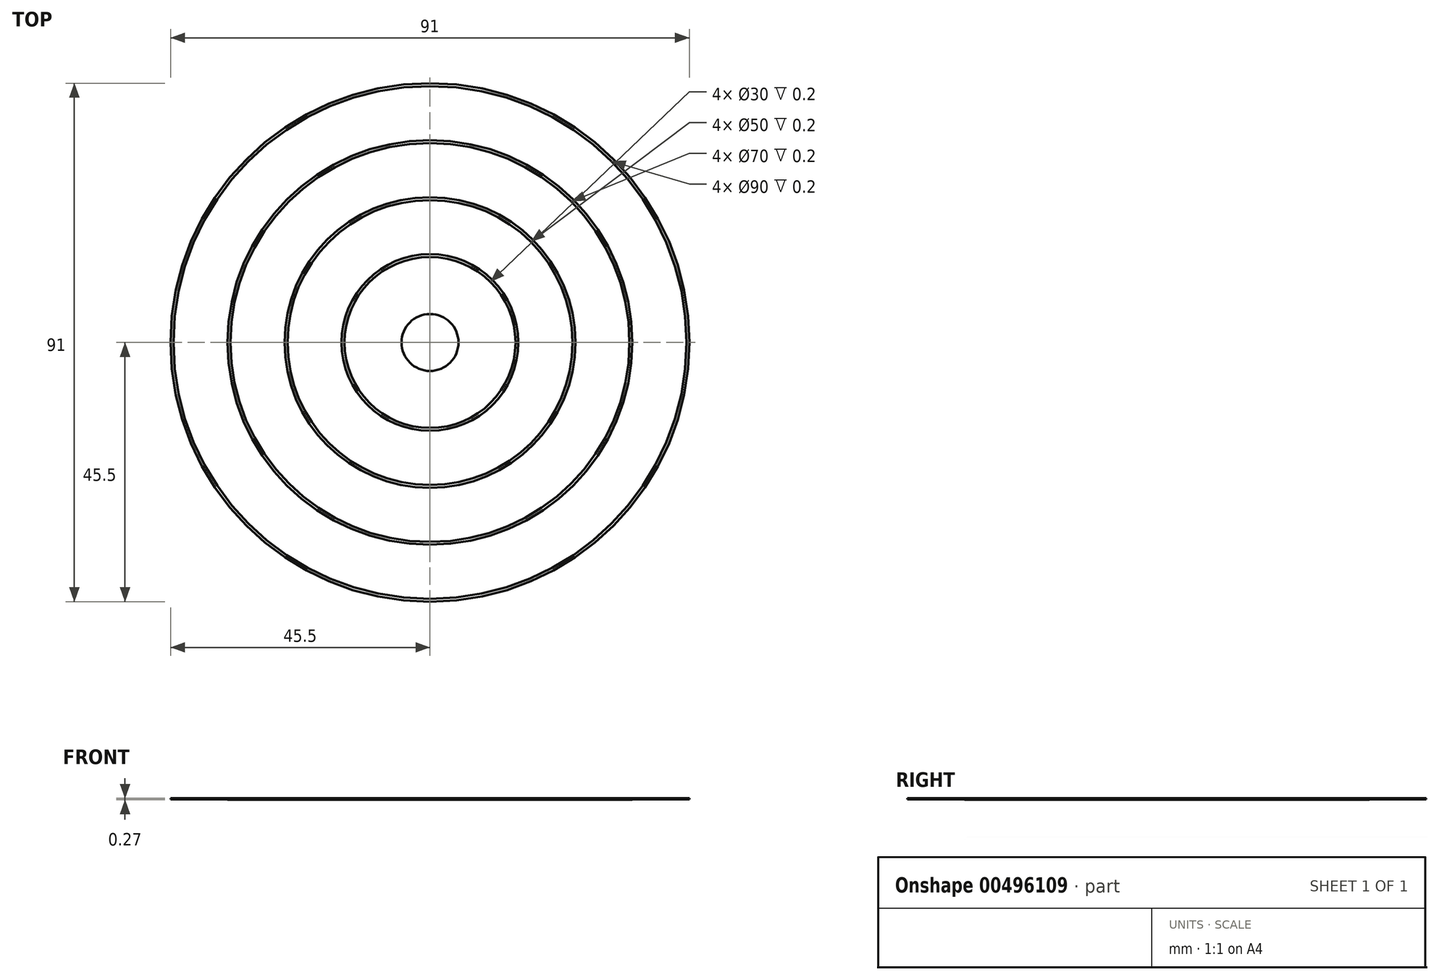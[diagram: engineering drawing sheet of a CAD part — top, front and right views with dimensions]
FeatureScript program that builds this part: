
annotation { "Feature Type Name" : "Feature", "Feature Type Description" : "" }
export const myFeature = defineFeature(function(context is Context, id is Id, definition is map)
    precondition{}
    {
        {
            var Q0;
            Q0=qCreatedBy(makeId("Right.planeOp"),FACE);
            var sketch = newSketch(context, id + "F0", { "sketchPlane" : qUnion([Q0])});
            skLineSegment(sketch, "E0.bottom", {"start": v(0, 0) * mm, "end": v(-5, 0) * mm});
            skLineSegment(sketch, "E0.top", {"start": v(0, 0.2) * mm, "end": v(-5, 0.2) * mm});
            skLineSegment(sketch, "E0.left", {"start": v(0, 0) * mm, "end": v(0, 0.2) * mm});
            skLineSegment(sketch, "E0.right", {"start": v(-5, 0) * mm, "end": v(-5, 0.2) * mm});
            skLineSegment(sketch, "E1.bottom", {"start": v(-15.5, 0.2) * mm, "end": v(-15, 0.2) * mm});
            skLineSegment(sketch, "E1.top", {"start": v(-15.5, 0) * mm, "end": v(-15, 0) * mm});
            skLineSegment(sketch, "E1.left", {"start": v(-15.5, 0.2) * mm, "end": v(-15.5, 0) * mm});
            skLineSegment(sketch, "E1.right", {"start": v(-15, 0.2) * mm, "end": v(-15, 0) * mm});
            skLineSegment(sketch, "E2.bottom", {"start": v(-25, 0) * mm, "end": v(-25.5, 0) * mm});
            skLineSegment(sketch, "E2.top", {"start": v(-25, 0.2) * mm, "end": v(-25.5, 0.2) * mm});
            skLineSegment(sketch, "E2.left", {"start": v(-25, 0) * mm, "end": v(-25, 0.2) * mm});
            skLineSegment(sketch, "E2.right", {"start": v(-25.5, 0) * mm, "end": v(-25.5, 0.2) * mm});
            skLineSegment(sketch, "E3.bottom", {"start": v(-35, -0.02) * mm, "end": v(-35.5, -0.02) * mm});
            skLineSegment(sketch, "E3.top", {"start": v(-35, 0.18) * mm, "end": v(-35.5, 0.18) * mm});
            skLineSegment(sketch, "E3.left", {"start": v(-35, -0.02) * mm, "end": v(-35, 0.18) * mm});
            skLineSegment(sketch, "E3.right", {"start": v(-35.5, -0.02) * mm, "end": v(-35.5, 0.18) * mm});
            skLineSegment(sketch, "E4.bottom", {"start": v(-45, 0.05) * mm, "end": v(-45.5, 0.05) * mm});
            skLineSegment(sketch, "E4.top", {"start": v(-45, 0.25) * mm, "end": v(-45.5, 0.25) * mm});
            skLineSegment(sketch, "E4.left", {"start": v(-45, 0.05) * mm, "end": v(-45, 0.25) * mm});
            skLineSegment(sketch, "E4.right", {"start": v(-45.5, 0.05) * mm, "end": v(-45.5, 0.25) * mm});
            skSolve(sketch);
        }
        {
            var Q0;
            Q0=makeQuery(id+"F0.imprint","IMPRINT",FACE,{"disambiguationData":[TD([[makeQuery(id+"F0.imprint","IMPRINT",EDGE,{"derivedFrom":sQuery(id+"F0.wireOp",EDGE,"E0.bottom")}),-1.0]])]});
            var Q1;
            Q1=makeQuery(id+"F0.imprint","IMPRINT",FACE,{"disambiguationData":[TD([[makeQuery(id+"F0.imprint","IMPRINT",EDGE,{"derivedFrom":sQuery(id+"F0.wireOp",EDGE,"E1.bottom")}),-1.0]])]});
            var Q2;
            Q2=makeQuery(id+"F0.imprint","IMPRINT",FACE,{"disambiguationData":[TD([[makeQuery(id+"F0.imprint","IMPRINT",EDGE,{"derivedFrom":sQuery(id+"F0.wireOp",EDGE,"E2.bottom")}),-1.0]])]});
            var Q3;
            Q3=makeQuery(id+"F0.imprint","IMPRINT",FACE,{"disambiguationData":[TD([[makeQuery(id+"F0.imprint","IMPRINT",EDGE,{"derivedFrom":sQuery(id+"F0.wireOp",EDGE,"E3.bottom")}),-1.0]])]});
            var Q4;
            Q4=makeQuery(id+"F0.imprint","IMPRINT",FACE,{"disambiguationData":[TD([[makeQuery(id+"F0.imprint","IMPRINT",EDGE,{"derivedFrom":sQuery(id+"F0.wireOp",EDGE,"E4.bottom")}),-1.0]])]});
            var Q5;
            Q5=sQuery(id+"F0.wireOp",EDGE,"E0.left");
            revolve(context, id + "F1", {"entities" : qUnion([Q0, Q1, Q2, Q3, Q4]), "axis" : qUnion([Q5]), "revolveType" : RevolveType.ONE_DIRECTION, "angle" : 360 * degree});
        }
    });
